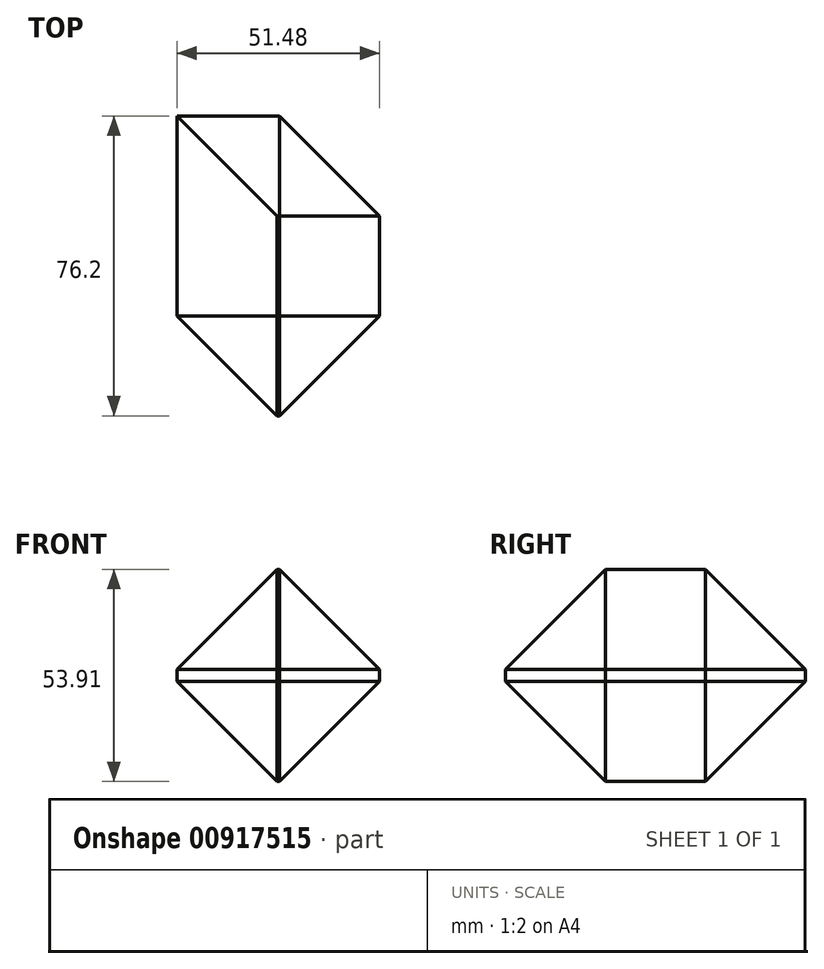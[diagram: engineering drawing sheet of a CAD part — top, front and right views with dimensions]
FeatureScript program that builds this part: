
annotation { "Feature Type Name" : "Feature", "Feature Type Description" : "" }
export const myFeature = defineFeature(function(context is Context, id is Id, definition is map)
    precondition{}
    {
        {
            var Q0;
            Q0=qCreatedBy(makeId("Front.planeOp"),FACE);
            var sketch = newSketch(context, id + "F0", { "sketchPlane" : qUnion([Q0])});
            skLineSegment(sketch, "E0.bottom", {"start": v(-26, 27.42) * mm, "end": v(25.5, 27.42) * mm});
            skLineSegment(sketch, "E0.top", {"start": v(-26, -26.5) * mm, "end": v(25.5, -26.5) * mm});
            skLineSegment(sketch, "E0.left", {"start": v(-26, 27.42) * mm, "end": v(-26, -26.5) * mm});
            skLineSegment(sketch, "E0.right", {"start": v(25.5, 27.42) * mm, "end": v(25.5, -26.5) * mm});
            skSolve(sketch);
        }
        {
            var Q0;
            Q0=makeQuery(id+"F0.imprint","IMPRINT",FACE,{"disambiguationData":[TD([[makeQuery(id+"F0.imprint","IMPRINT",EDGE,{"derivedFrom":sQuery(id+"F0.wireOp",EDGE,"E0.bottom")}),-1.0]])]});
            extrude(context, id + "F1", {"entities" : qUnion([Q0]), "depth" : 76.2 * mm, "offsetDistance" : 25.4 * mm});
        }
        {
            var Q0;
            Q0=makeQuery(id+"F1.opExtrude","SWEPT_FACE",FACE,{"disambiguationData":[OSD([sQuery(id+"F0.wireOp",EDGE,"E0.bottom")])]});
            var Q1;
            Q1=makeQuery(id+"F1.opExtrude","CAP_FACE",FACE,{"disambiguationData":[OSD([sQuery(id+"F0.wireOp",EDGE,"E0.bottom"),sQuery(id+"F0.wireOp",EDGE,"E0.top"),sQuery(id+"F0.wireOp",EDGE,"E0.left"),sQuery(id+"F0.wireOp",EDGE,"E0.right")])],"isStart":false});
            var Q2;
            Q2=makeQuery(id+"F1.opExtrude","SWEPT_FACE",FACE,{"disambiguationData":[OSD([sQuery(id+"F0.wireOp",EDGE,"E0.top")])]});
            var Q3;
            Q3=makeQuery(id+"F1.opExtrude","SWEPT_EDGE",EDGE,{"disambiguationData":[OSD([sQuery(id+"F0.wireOp",EDGE,"E0.top"),sQuery(id+"F0.wireOp",EDGE,"E0.right")])]});
            var Q4;
            Q4=makeQuery(id+"F1.opExtrude","SWEPT_EDGE",EDGE,{"disambiguationData":[OSD([sQuery(id+"F0.wireOp",EDGE,"E0.bottom"),sQuery(id+"F0.wireOp",EDGE,"E0.right")])]});
            var Q5;
            Q5=makeQuery(id+"F1.opExtrude","CAP_EDGE",EDGE,{"disambiguationData":[OSD([sQuery(id+"F0.wireOp",EDGE,"E0.right")])],"isStart":true});
            var Q6;
            Q6=makeQuery(id+"F1.opExtrude","SWEPT_EDGE",EDGE,{"disambiguationData":[OSD([sQuery(id+"F0.wireOp",EDGE,"E0.bottom"),sQuery(id+"F0.wireOp",EDGE,"E0.left")])]});
            chamfer(context, id + "F2", {"entities" : qUnion([Q0, Q1, Q2, Q3, Q4, Q5, Q6]), "width" : 25.4 * mm, "tangentPropagation" : true});
        }
    });
